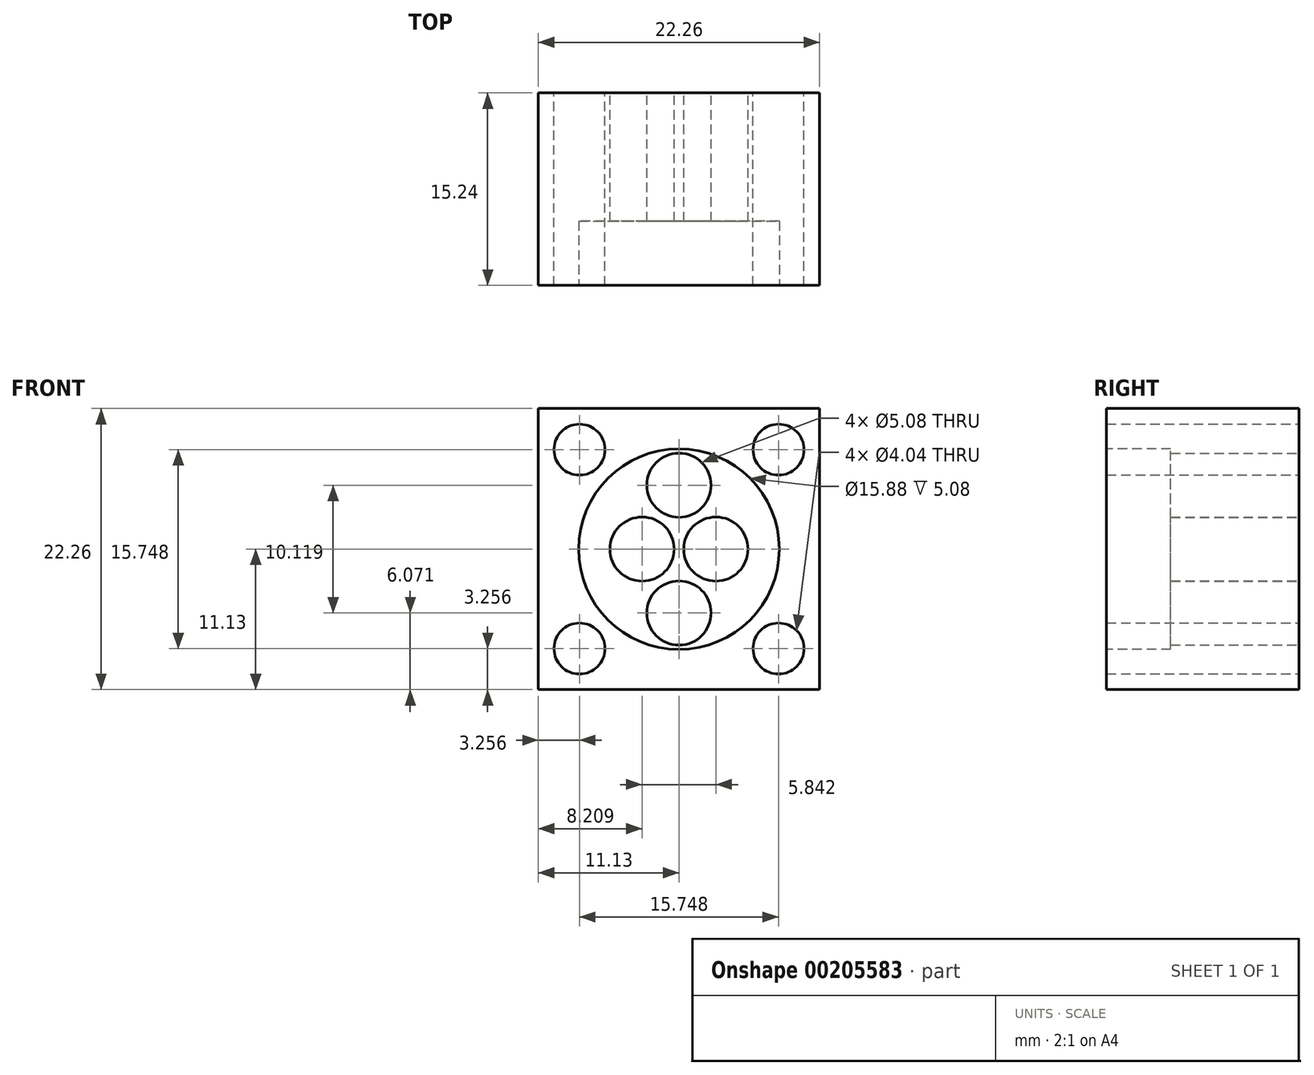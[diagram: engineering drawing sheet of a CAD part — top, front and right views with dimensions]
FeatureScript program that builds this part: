
annotation { "Feature Type Name" : "Feature", "Feature Type Description" : "" }
export const myFeature = defineFeature(function(context is Context, id is Id, definition is map)
    precondition{}
    {
        {
            var Q0;
            Q0=qCreatedBy(makeId("Front.planeOp"),FACE);
            var sketch = newSketch(context, id + "F0", { "sketchPlane" : qUnion([Q0])});
            skCircle(sketch, "E0", {"center": v(-2.92, 0) * mm, "radius": 2.54 * mm});
            skCircle(sketch, "E1", {"center": v(2.92, 0) * mm, "radius": 2.54 * mm});
            skCircle(sketch, "E2", {"center": v(0, 5.06) * mm, "radius": 2.54 * mm});
            skCircle(sketch, "E3", {"center": v(0, -5.06) * mm, "radius": 2.54 * mm});
            skCircle(sketch, "E4", {"center": v(7.87, 7.87) * mm, "radius": 2.02 * mm});
            skLineSegment(sketch, "E5.bottom", {"start": v(-11.13, 11.13) * mm, "end": v(11.13, 11.13) * mm});
            skLineSegment(sketch, "E5.top", {"start": v(-11.13, -11.13) * mm, "end": v(11.13, -11.13) * mm});
            skLineSegment(sketch, "E5.left", {"start": v(-11.13, 11.13) * mm, "end": v(-11.13, -11.13) * mm});
            skLineSegment(sketch, "E5.right", {"start": v(11.13, 11.13) * mm, "end": v(11.13, -11.13) * mm});
            skPoint(sketch, "E5.middle", {"position": v(0, 0) * mm});
            skCircle(sketch, "E6", {"center": v(-7.87, 7.87) * mm, "radius": 2.02 * mm});
            skCircle(sketch, "E7", {"center": v(-7.87, -7.87) * mm, "radius": 2.02 * mm});
            skCircle(sketch, "E8", {"center": v(7.87, -7.87) * mm, "radius": 2.02 * mm});
            skSolve(sketch);
        }
        {
            var Q0;
            Q0=qSketchRegion(id+"F0",true);
            extrude(context, id + "F1", {"entities" : qUnion([Q0]), "depth" : 15.24 * mm});
        }
        {
            var Q0;
            Q0=makeQuery(id+"F1.opExtrude","CAP_FACE",FACE,{"disambiguationData":[OSD([sQuery(id+"F0.wireOp",EDGE,"E0"),sQuery(id+"F0.wireOp",EDGE,"E1"),sQuery(id+"F0.wireOp",EDGE,"E2"),sQuery(id+"F0.wireOp",EDGE,"E3"),sQuery(id+"F0.wireOp",EDGE,"E4"),sQuery(id+"F0.wireOp",EDGE,"E5.bottom"),sQuery(id+"F0.wireOp",EDGE,"E5.top"),sQuery(id+"F0.wireOp",EDGE,"E5.left"),sQuery(id+"F0.wireOp",EDGE,"E5.right"),sQuery(id+"F0.wireOp",EDGE,"E6"),sQuery(id+"F0.wireOp",EDGE,"E7"),sQuery(id+"F0.wireOp",EDGE,"E8")])],"isStart":false});
            var sketch = newSketch(context, id + "F2", { "sketchPlane" : qUnion([Q0])});
            skCircle(sketch, "E9", {"center": v(0, 0) * mm, "radius": 7.94 * mm});
            skSolve(sketch);
        }
        {
            var Q0;
            Q0=qSketchRegion(id+"F2",true);
            extrude(context, id + "F3", {"entities" : qUnion([Q0]), "operationType" : NewBodyOperationType.REMOVE, "oppositeDirection" : true, "depth" : 5.08 * mm});
        }
    });
